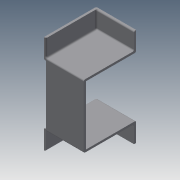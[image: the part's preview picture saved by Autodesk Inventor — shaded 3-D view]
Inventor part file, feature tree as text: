
AUTODESK INVENTOR PART (.ipt)
format: ipt  version: 2013 (Build 170138000, 138)  size: 204,288 bytes
history: native  units: mm
features: extrude x8, sketch x8, fillet x2
ambient origin geometry x8: Origin, YZ Plane, XZ Plane, XY Plane, X Axis, Y Axis, Z Axis, Center Point
bodies: Solid1 (feature_tree)
feature tree (18):
  extrude  "Extrusion1"  Depth=44.2mm
  extrude  "Extrusion2"  Depth=1.5mm
  sketch  "Sketch3"  dims[d5=1.5mm d6=35.0mm d7=0.0mm]
  extrude  "Extrusion3"  Depth=35.0mm TaperAngle=0.0deg
  extrude  "Extrusion4"  Depth=1.5mm
  extrude  "Extrusion5"  Depth=12.0mm TaperAngle=0.0deg
  extrude  "Extrusion6"  Depth=1.5mm
  extrude  "Extrusion7"  Depth=1.5mm
  fillet  "Fillet1"  Radius=12.0mm
  fillet  "Fillet2"  Radius=1.0mm
  extrude  "Extrusion8"  Depth=1.5mm TaperAngle=0.0deg
  sketch  "Sketch1"  dims[d0=27.8mm d1=44.2mm]
  sketch  "Sketch2"  dims[d2=1.5mm d3=0.0mm d4=1.5mm]
  sketch  "Sketch4"  dims[d8=1.5mm d9=1.5mm]
  sketch  "Sketch5"  dims[d10=12.0mm d11=0.0mm d12=12.0mm d13=0.0mm]
  sketch  "Sketch6"  dims[d14=1.5mm d15=0.0mm d16=1.5mm]
  sketch  "Sketch7"  dims[d17=12.0mm d18=0.0mm d19=1.5mm d20=12.0mm d21=0.0mm d22=1.0mm]
  sketch  "Sketch8"  dims[d23=1.0mm d24=1.5mm d25=0.0mm]
